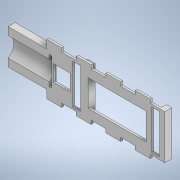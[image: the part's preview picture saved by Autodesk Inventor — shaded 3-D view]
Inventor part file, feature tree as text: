
AUTODESK INVENTOR PART (.ipt)
format: ipt  version: 2022 (Build 260153000, 153)  size: 269,824 bytes
history: native  units: mm
features: sketch x7, extrude x6
ambient origin geometry x8: Origin, YZ Plane, XZ Plane, XY Plane, X Axis, Y Axis, Z Axis, Center Point
bodies: Solid1 (feature_tree)
feature tree (13):
  extrude  "Extrusion1"  Depth=24.36mm
  extrude  "Extrusion2"  Depth=24.36mm
  extrude  "Extrusion3"  Depth=23.64mm
  extrude  "Extrusion6"  Depth=23.64mm
  extrude  "Extrusion7"  Depth=6.085mm
  sketch  "Sketch11"  dims[d13=6.085mm d14=24.36mm]
  extrude  "Extrusion8"  Depth=24.36mm
  sketch  "Sketch1"  dims[d0=84.0mm d1=24.36mm]
  sketch  "Sketch2"  dims[d2=23.64mm d3=24.36mm]
  sketch  "Sketch3"  dims[d5=24.36mm d8=23.64mm]
  sketch  "Sketch9"  dims[d9=71.83mm d10=23.64mm]
  sketch  "Sketch10"  dims[d11=6.085mm d12=6.085mm]
  sketch  "Sketch12"  dims[d15=23.64mm d16=24.36mm d17=23.64mm d18=24.36mm d19=23.64mm d20=24.36mm d21=23.64mm d22=23.64mm d23=3.25mm d24=0.0mm d25=4.17mm d26=4.1mm d27=45.05mm d28=19.475mm d29=10.94mm d30=26.36mm d31=27.24mm d32=42.15mm d33=28.82mm d34=64.14mm d35=12.64mm d36=9.93mm d37=67.36mm d38=43.06mm d39=94.46mm d40=20.47mm d41=64.14mm d42=12.64mm d43=3.845mm d44=8.77mm d45=4.0mm d46=0.0mm d47=37.0mm d48=23.5mm d49=2.0mm d50=4.0mm d51=0.0mm d64=0.0mm d65=13.5mm d66=13.5mm d67=66.6mm d68=11.25mm d69=0.0mm d70=42.0mm d71=37.0mm d72=20.75mm d73=66.6mm d74=0.0mm d75=0.0mm d76=0.0mm d77=0.0mm d78=0.0mm d79=0.0mm d80=0.0mm d81=0.0mm d82=0.0mm d83=11.25mm d84=0.0mm d56=0.5mm d57=0.872665mm d58=0.5mm d59=0.872665mm d85=0.5mm d86=0.872665mm]
